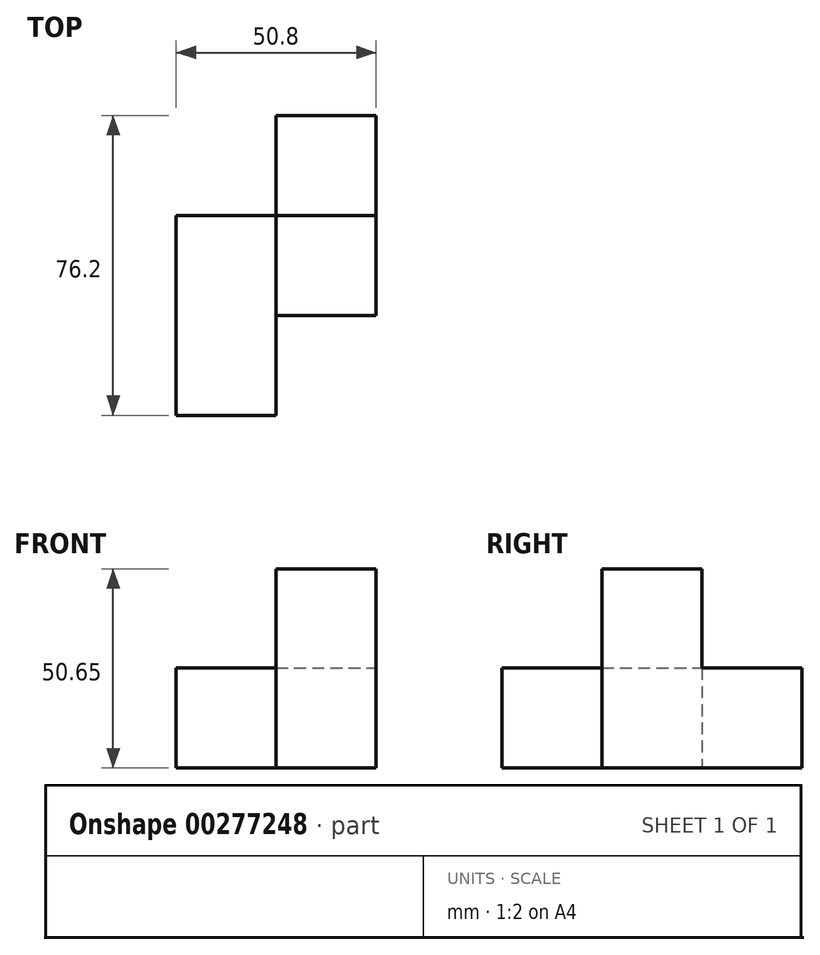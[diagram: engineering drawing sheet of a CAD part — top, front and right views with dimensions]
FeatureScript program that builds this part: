
annotation { "Feature Type Name" : "Feature", "Feature Type Description" : "" }
export const myFeature = defineFeature(function(context is Context, id is Id, definition is map)
    precondition{}
    {
        {
            var Q0;
            Q0=qCreatedBy(makeId("Top.planeOp"),FACE);
            var sketch = newSketch(context, id + "F0", { "sketchPlane" : qUnion([Q0])});
            skLineSegment(sketch, "E0", {"start": v(0, 0) * mm, "end": v(25.4, 0) * mm});
            skLineSegment(sketch, "E1", {"start": v(25.4, 0) * mm, "end": v(25.4, 25.4) * mm});
            skLineSegment(sketch, "E2", {"start": v(25.4, 25.4) * mm, "end": v(0, 25.4) * mm});
            skLineSegment(sketch, "E3", {"start": v(0, 25.4) * mm, "end": v(0, 0) * mm});
            skLineSegment(sketch, "E4", {"start": v(0, 25.4) * mm, "end": v(0, 50.8) * mm});
            skLineSegment(sketch, "E5", {"start": v(0, 50.8) * mm, "end": v(25.4, 50.8) * mm});
            skLineSegment(sketch, "E6", {"start": v(25.4, 50.8) * mm, "end": v(25.4, 25.4) * mm});
            skLineSegment(sketch, "E7", {"start": v(0, 25.4) * mm, "end": v(-25.4, 25.4) * mm});
            skLineSegment(sketch, "E8", {"start": v(-25.4, 25.4) * mm, "end": v(-25.4, 0) * mm});
            skLineSegment(sketch, "E9", {"start": v(-25.4, 0) * mm, "end": v(0, 0) * mm});
            skLineSegment(sketch, "E10", {"start": v(-25.4, 0) * mm, "end": v(-25.4, -25.4) * mm});
            skLineSegment(sketch, "E11", {"start": v(-25.4, -25.4) * mm, "end": v(0, -25.4) * mm});
            skLineSegment(sketch, "E12", {"start": v(0, -25.4) * mm, "end": v(0, 0) * mm});
            skSolve(sketch);
        }
        {
            var Q0;
            Q0=makeQuery(id+"F0.imprint","IMPRINT",FACE,{"disambiguationData":[TD([[makeQuery(id+"F0.imprint","IMPRINT",EDGE,{"derivedFrom":sQuery(id+"F0.wireOp",EDGE,"E9")}),-1.0]])]});
            var Q1;
            Q1=makeQuery(id+"F0.imprint","IMPRINT",FACE,{"disambiguationData":[TD([[makeQuery(id+"F0.imprint","IMPRINT",EDGE,{"derivedFrom":sQuery(id+"F0.wireOp",EDGE,"E0")}),1.0]])]});
            var Q2;
            Q2=makeQuery(id+"F0.imprint","IMPRINT",FACE,{"disambiguationData":[TD([[makeQuery(id+"F0.imprint","IMPRINT",EDGE,{"derivedFrom":sQuery(id+"F0.wireOp",EDGE,"E3")}),-1.0]])]});
            var Q3;
            Q3=makeQuery(id+"F0.imprint","IMPRINT",FACE,{"disambiguationData":[TD([[makeQuery(id+"F0.imprint","IMPRINT",EDGE,{"derivedFrom":sQuery(id+"F0.wireOp",EDGE,"E9")}),-1.0]])]});
            var Q4;
            Q4=makeQuery(id+"F0.imprint","IMPRINT",FACE,{"disambiguationData":[TD([[makeQuery(id+"F0.imprint","IMPRINT",EDGE,{"derivedFrom":sQuery(id+"F0.wireOp",EDGE,"E0")}),1.0]])]});
            var Q5;
            Q5=makeQuery(id+"F0.imprint","IMPRINT",FACE,{"disambiguationData":[TD([[makeQuery(id+"F0.imprint","IMPRINT",EDGE,{"derivedFrom":sQuery(id+"F0.wireOp",EDGE,"E3")}),-1.0]])]});
            var Q6;
            Q6=makeQuery(id+"F0.imprint","IMPRINT",FACE,{"disambiguationData":[TD([[makeQuery(id+"F0.imprint","IMPRINT",EDGE,{"derivedFrom":sQuery(id+"F0.wireOp",EDGE,"E2")}),-1.0]])]});
            extrude(context, id + "F1", {"entities" : qUnion([Q0, Q1, Q2, Q3, Q4, Q5, Q6]), "depth" : 25.4 * mm});
        }
        {
            var Q0;
            Q0=qCreatedBy(makeId("Right.planeOp"),FACE);
            var sketch = newSketch(context, id + "F2", { "sketchPlane" : qUnion([Q0])});
            skLineSegment(sketch, "E13", {"start": v(0, 25.25) * mm, "end": v(0, 50.65) * mm});
            skLineSegment(sketch, "E14", {"start": v(0, 50.65) * mm, "end": v(25.4, 50.65) * mm});
            skLineSegment(sketch, "E15", {"start": v(25.4, 50.65) * mm, "end": v(25.4, 25.25) * mm});
            skLineSegment(sketch, "E16", {"start": v(25.4, 25.25) * mm, "end": v(0, 25.25) * mm});
            skSolve(sketch);
        }
        {
            var Q0;
            Q0 = qSketchRegion(id + "F2", true);
            extrude(context, id + "F3", {"entities" : qUnion([Q0]), "operationType" : NewBodyOperationType.ADD, "depth" : 25.4 * mm});
        }
    });
